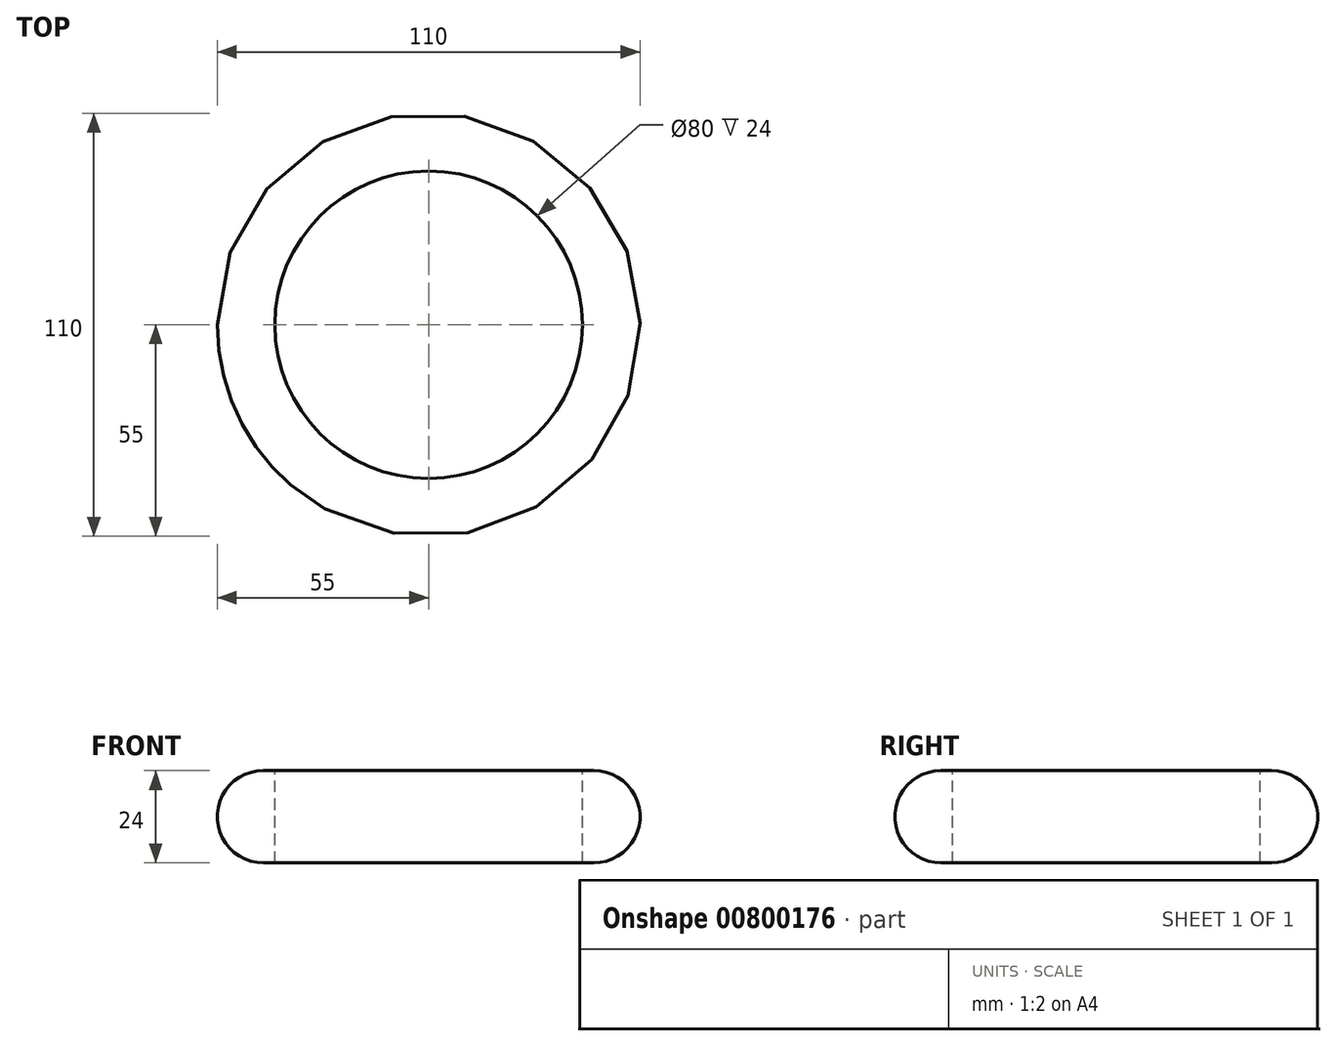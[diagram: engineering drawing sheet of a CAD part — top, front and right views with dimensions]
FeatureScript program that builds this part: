
annotation { "Feature Type Name" : "Feature", "Feature Type Description" : "" }
export const myFeature = defineFeature(function(context is Context, id is Id, definition is map)
    precondition{}
    {
        {
            var Q0;
            Q0=qCreatedBy(makeId("Top.planeOp"),FACE);
            var sketch = newSketch(context, id + "F0", { "sketchPlane" : qUnion([Q0])});
            skCircle(sketch, "E0", {"center": v(0, 0) * mm, "radius": 40 * mm});
            skSolve(sketch);
        }
        {
            var Q0;
            Q0=qCreatedBy(makeId("Front.planeOp"),FACE);
            var sketch = newSketch(context, id + "F1", { "sketchPlane" : qUnion([Q0])});
            skArc(sketch, "E1", {"start": v(-43, 12) * mm, "mid": v(-55, 0) * mm, "end": v(-43, -12) * mm});
            skLineSegment(sketch, "E2", {"start": v(-43, 12) * mm, "end": v(-40, 12) * mm});
            skLineSegment(sketch, "E3", {"start": v(-40, 12) * mm, "end": v(-40, -12) * mm});
            skLineSegment(sketch, "E4", {"start": v(-40, -12) * mm, "end": v(-43, -12) * mm});
            skSolve(sketch);
        }
        {
            var Q0;
            Q0=qSketchRegion(id+"F1",true);
            var Q1;
            Q1=qConstructionFilter(qBodyType(qCreatedBy(id+"F0",EDGE),BodyType.WIRE),ConstructionObject.NO);
            sweep(context, id + "F2", {"profiles" : qUnion([Q0]), "path" : qUnion([Q1])});
        }
    });
